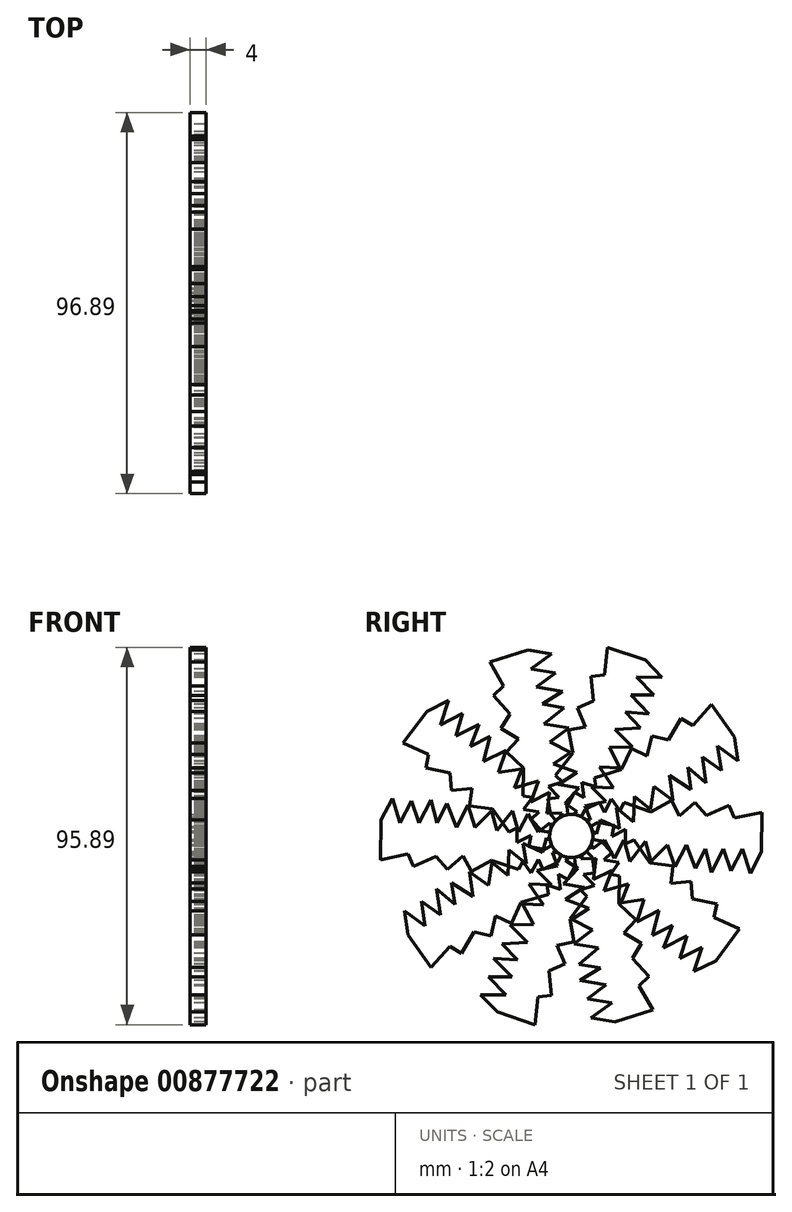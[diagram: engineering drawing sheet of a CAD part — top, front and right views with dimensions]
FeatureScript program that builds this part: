
annotation { "Feature Type Name" : "Feature", "Feature Type Description" : "" }
export const myFeature = defineFeature(function(context is Context, id is Id, definition is map)
    precondition{}
    {
        {
            var Q0;
            Q0=qCreatedBy(makeId("Right.planeOp"),FACE);
            var sketch = newSketch(context, id + "F0", { "sketchPlane" : qUnion([Q0])});
            skLineSegment(sketch, "E0", {"start": v(64.04, -37.62) * mm, "end": v(61.2, -43.05) * mm});
            skLineSegment(sketch, "E1", {"start": v(61.2, -43.05) * mm, "end": v(59.23, -36.88) * mm});
            skLineSegment(sketch, "E2", {"start": v(59.23, -36.88) * mm, "end": v(56.32, -42.46) * mm});
            skLineSegment(sketch, "E3", {"start": v(56.32, -42.46) * mm, "end": v(54.42, -36.88) * mm});
            skLineSegment(sketch, "E4", {"start": v(54.42, -36.88) * mm, "end": v(51.35, -42.76) * mm});
            skLineSegment(sketch, "E5", {"start": v(51.35, -42.76) * mm, "end": v(49.86, -36.88) * mm});
            skLineSegment(sketch, "E6", {"start": v(49.86, -36.88) * mm, "end": v(47.28, -41.82) * mm});
            skLineSegment(sketch, "E7", {"start": v(47.28, -41.82) * mm, "end": v(44.93, -35.77) * mm});
            skLineSegment(sketch, "E8", {"start": v(44.93, -35.77) * mm, "end": v(41.99, -41.4) * mm});
            skLineSegment(sketch, "E9", {"start": v(41.99, -41.4) * mm, "end": v(40.13, -35.77) * mm});
            skLineSegment(sketch, "E10", {"start": v(40.13, -35.77) * mm, "end": v(35.93, -39.97) * mm});
            skLineSegment(sketch, "E11", {"start": v(35.93, -39.97) * mm, "end": v(34.58, -34.91) * mm});
            skLineSegment(sketch, "E12", {"start": v(34.58, -34.91) * mm, "end": v(30.63, -39.97) * mm});
            skLineSegment(sketch, "E13", {"start": v(30.63, -39.97) * mm, "end": v(29.15, -34.54) * mm});
            skLineSegment(sketch, "E14", {"start": v(29.15, -34.54) * mm, "end": v(26.72, -39.2) * mm});
            skLineSegment(sketch, "E15", {"start": v(26.72, -39.2) * mm, "end": v(24.1, -34.54) * mm});
            skLineSegment(sketch, "E16", {"start": v(24.1, -34.54) * mm, "end": v(21.14, -36.88) * mm});
            skLineSegment(sketch, "E17", {"start": v(21.14, -36.88) * mm, "end": v(20.03, -33.06) * mm});
            skLineSegment(sketch, "E18", {"start": v(20.03, -33.06) * mm, "end": v(15.72, -36.88) * mm});
            skLineSegment(sketch, "E19", {"start": v(15.72, -36.88) * mm, "end": v(15.72, -33.56) * mm});
            skLineSegment(sketch, "E20", {"start": v(19.24, -26.81) * mm, "end": v(22.87, -25.05) * mm});
            skLineSegment(sketch, "E21", {"start": v(22.87, -25.05) * mm, "end": v(24.1, -27.58) * mm});
            skLineSegment(sketch, "E22", {"start": v(24.1, -27.58) * mm, "end": v(25.91, -24.12) * mm});
            skLineSegment(sketch, "E23", {"start": v(25.91, -24.12) * mm, "end": v(28.04, -27.15) * mm});
            skLineSegment(sketch, "E24", {"start": v(28.04, -27.15) * mm, "end": v(29.15, -25.02) * mm});
            skLineSegment(sketch, "E25", {"start": v(29.15, -25.02) * mm, "end": v(35.93, -27.4) * mm});
            skLineSegment(sketch, "E26", {"start": v(35.93, -27.4) * mm, "end": v(41.11, -24.56) * mm});
            skLineSegment(sketch, "E27", {"start": v(41.11, -24.56) * mm, "end": v(43.24, -28.44) * mm});
            skLineSegment(sketch, "E28", {"start": v(43.24, -28.44) * mm, "end": v(47.15, -25.05) * mm});
            skLineSegment(sketch, "E29", {"start": v(47.15, -25.05) * mm, "end": v(50.04, -28.38) * mm});
            skLineSegment(sketch, "E30", {"start": v(50.04, -28.38) * mm, "end": v(55.78, -25.79) * mm});
            skLineSegment(sketch, "E31", {"start": v(55.78, -25.79) * mm, "end": v(57.22, -28.97) * mm});
            skLineSegment(sketch, "E32", {"start": v(57.22, -28.97) * mm, "end": v(64.16, -27.52) * mm});
            skLineSegment(sketch, "E33", {"start": v(64.16, -27.52) * mm, "end": v(64.04, -37.62) * mm});
            skLineSegment(sketch, "E34", {"start": v(15.72, -33.56) * mm, "end": v(19.24, -26.81) * mm});
            skSolve(sketch);
        }
        {
            var Q0;
            Q0=makeQuery(id+"F0.imprint","IMPRINT",FACE,{"disambiguationData":[TD([[makeQuery(id+"F0.imprint","IMPRINT",EDGE,{"derivedFrom":sQuery(id+"F0.wireOp",EDGE,"E0")}),-1.0]])]});
            extrude(context, id + "F1", {"entities" : qUnion([Q0]), "depth" : 4 * mm, "offsetDistance" : 25 * mm});
        }
        {
            var Q0;
            Q0=makeQuery(id+"F1.opExtrude","SWEPT_BODY",BODY,{"disambiguationData":[OSD([sQuery(id+"F0.wireOp",EDGE,"E0"),sQuery(id+"F0.wireOp",EDGE,"E1"),sQuery(id+"F0.wireOp",EDGE,"E2"),sQuery(id+"F0.wireOp",EDGE,"E3"),sQuery(id+"F0.wireOp",EDGE,"E4"),sQuery(id+"F0.wireOp",EDGE,"E5"),sQuery(id+"F0.wireOp",EDGE,"E6"),sQuery(id+"F0.wireOp",EDGE,"E7"),sQuery(id+"F0.wireOp",EDGE,"E8"),sQuery(id+"F0.wireOp",EDGE,"E9"),sQuery(id+"F0.wireOp",EDGE,"E10"),sQuery(id+"F0.wireOp",EDGE,"E11"),sQuery(id+"F0.wireOp",EDGE,"E12"),sQuery(id+"F0.wireOp",EDGE,"E13"),sQuery(id+"F0.wireOp",EDGE,"E14"),sQuery(id+"F0.wireOp",EDGE,"E15"),sQuery(id+"F0.wireOp",EDGE,"E16"),sQuery(id+"F0.wireOp",EDGE,"E17"),sQuery(id+"F0.wireOp",EDGE,"E18"),sQuery(id+"F0.wireOp",EDGE,"E19"),sQuery(id+"F0.wireOp",EDGE,"E20"),sQuery(id+"F0.wireOp",EDGE,"E21"),sQuery(id+"F0.wireOp",EDGE,"E22"),sQuery(id+"F0.wireOp",EDGE,"E23"),sQuery(id+"F0.wireOp",EDGE,"E24"),sQuery(id+"F0.wireOp",EDGE,"E25"),sQuery(id+"F0.wireOp",EDGE,"E26"),sQuery(id+"F0.wireOp",EDGE,"E27"),sQuery(id+"F0.wireOp",EDGE,"E28"),sQuery(id+"F0.wireOp",EDGE,"E29"),sQuery(id+"F0.wireOp",EDGE,"E30"),sQuery(id+"F0.wireOp",EDGE,"E31"),sQuery(id+"F0.wireOp",EDGE,"E32"),sQuery(id+"F0.wireOp",EDGE,"E33"),sQuery(id+"F0.wireOp",EDGE,"E34")])]});
            var Q1;
            Q1=makeQuery(id+"F1.opExtrude","SWEPT_EDGE",EDGE,{"disambiguationData":[OSD([sQuery(id+"F0.wireOp",EDGE,"E19"),sQuery(id+"F0.wireOp",EDGE,"E34")])]});
            circularPattern(context, id + "F2", {"entities" : qUnion([Q0]), "axis" : qUnion([Q1]), "angle" : 360 * degree, "instanceCount" : 10, "equalSpace" : true});
        }
        {
            var Q0;
            Q0=makeQuery(id+"F2.opPattern","COPY",FACE,{"derivedFrom":makeQuery(id+"F1.opExtrude","CAP_FACE",FACE,{"disambiguationData":[OSD([sQuery(id+"F0.wireOp",EDGE,"E0"),sQuery(id+"F0.wireOp",EDGE,"E1"),sQuery(id+"F0.wireOp",EDGE,"E2"),sQuery(id+"F0.wireOp",EDGE,"E3"),sQuery(id+"F0.wireOp",EDGE,"E4"),sQuery(id+"F0.wireOp",EDGE,"E5"),sQuery(id+"F0.wireOp",EDGE,"E6"),sQuery(id+"F0.wireOp",EDGE,"E7"),sQuery(id+"F0.wireOp",EDGE,"E8"),sQuery(id+"F0.wireOp",EDGE,"E9"),sQuery(id+"F0.wireOp",EDGE,"E10"),sQuery(id+"F0.wireOp",EDGE,"E11"),sQuery(id+"F0.wireOp",EDGE,"E12"),sQuery(id+"F0.wireOp",EDGE,"E13"),sQuery(id+"F0.wireOp",EDGE,"E14"),sQuery(id+"F0.wireOp",EDGE,"E15"),sQuery(id+"F0.wireOp",EDGE,"E16"),sQuery(id+"F0.wireOp",EDGE,"E17"),sQuery(id+"F0.wireOp",EDGE,"E18"),sQuery(id+"F0.wireOp",EDGE,"E19"),sQuery(id+"F0.wireOp",EDGE,"E20"),sQuery(id+"F0.wireOp",EDGE,"E21"),sQuery(id+"F0.wireOp",EDGE,"E22"),sQuery(id+"F0.wireOp",EDGE,"E23"),sQuery(id+"F0.wireOp",EDGE,"E24"),sQuery(id+"F0.wireOp",EDGE,"E25"),sQuery(id+"F0.wireOp",EDGE,"E26"),sQuery(id+"F0.wireOp",EDGE,"E27"),sQuery(id+"F0.wireOp",EDGE,"E28"),sQuery(id+"F0.wireOp",EDGE,"E29"),sQuery(id+"F0.wireOp",EDGE,"E30"),sQuery(id+"F0.wireOp",EDGE,"E31"),sQuery(id+"F0.wireOp",EDGE,"E32"),sQuery(id+"F0.wireOp",EDGE,"E33"),sQuery(id+"F0.wireOp",EDGE,"E34")])],"isStart":false}),"instanceName":"1"});
            var sketch = newSketch(context, id + "F3", { "sketchPlane" : qUnion([Q0])});
            skCircle(sketch, "E35", {"center": v(15.72, -33.56) * mm, "radius": 5.5 * mm});
            skSolve(sketch);
        }
        {
            var Q0;
            Q0 = qSketchRegion(id + "F3", true);
            extrude(context, id + "F4", {"entities" : qUnion([Q0]), "operationType" : NewBodyOperationType.REMOVE, "oppositeDirection" : true, "depth" : 25 * mm, "offsetDistance" : 25 * mm});
        }
    });
